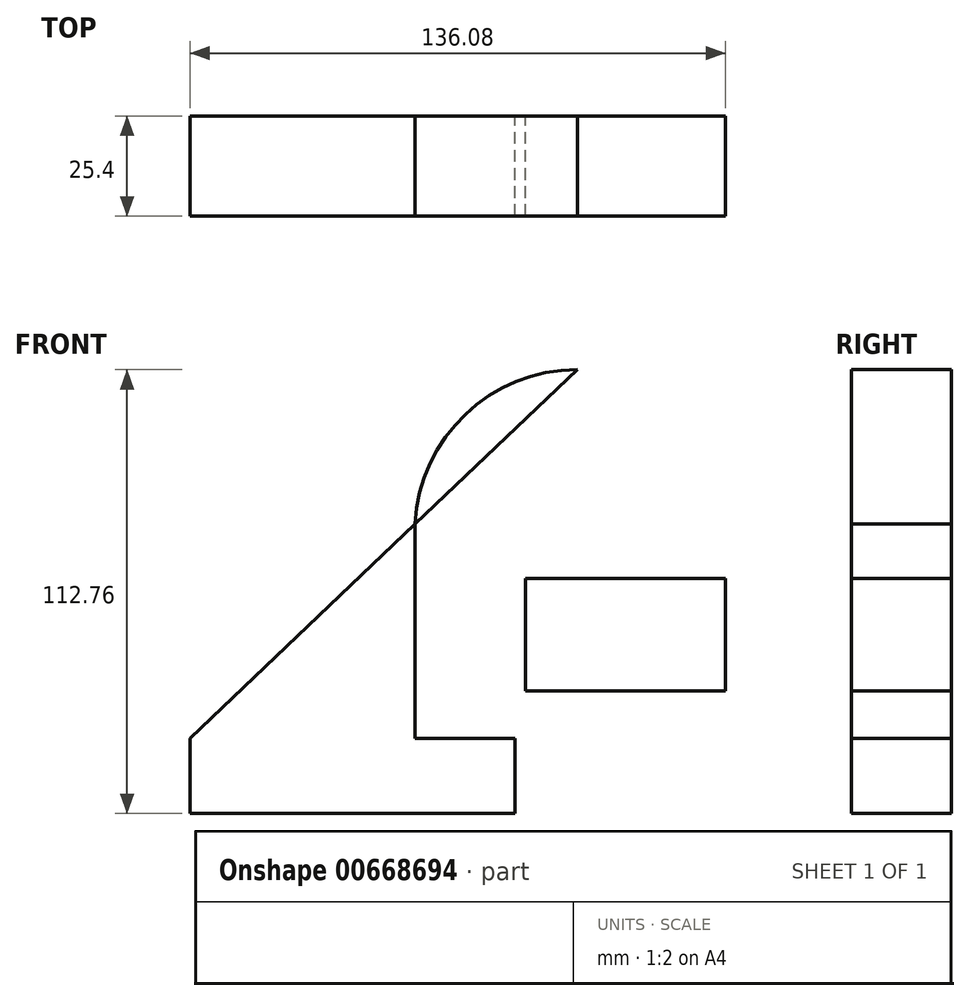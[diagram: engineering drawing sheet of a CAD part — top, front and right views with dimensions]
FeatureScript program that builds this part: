
annotation { "Feature Type Name" : "Feature", "Feature Type Description" : "" }
export const myFeature = defineFeature(function(context is Context, id is Id, definition is map)
    precondition{}
    {
        {
            var Q0;
            Q0=qCreatedBy(makeId("Front.planeOp"),FACE);
            var sketch = newSketch(context, id + "F0", { "sketchPlane" : qUnion([Q0])});
            skLineSegment(sketch, "E0.bottom", {"start": v(41.28, -9.52) * mm, "end": v(-41.28, -9.53) * mm});
            skLineSegment(sketch, "E0.top", {"start": v(41.27, 9.53) * mm, "end": v(-41.28, 9.53) * mm});
            skLineSegment(sketch, "E0.left", {"start": v(41.28, -9.53) * mm, "end": v(41.28, 9.53) * mm});
            skLineSegment(sketch, "E0.right", {"start": v(-41.28, -9.53) * mm, "end": v(-41.28, 9.53) * mm});
            skPoint(sketch, "E0.middle", {"position": v(0, 0) * mm});
            skLineSegment(sketch, "E1.bottom", {"start": v(94.8, 21.6) * mm, "end": v(44, 21.6) * mm});
            skLineSegment(sketch, "E1.top", {"start": v(94.8, 50.17) * mm, "end": v(44, 50.17) * mm});
            skLineSegment(sketch, "E1.left", {"start": v(94.8, 21.6) * mm, "end": v(94.8, 50.17) * mm});
            skLineSegment(sketch, "E1.right", {"start": v(44, 21.6) * mm, "end": v(44, 50.17) * mm});
            skPoint(sketch, "E1.middle", {"position": v(69.4, 35.89) * mm});
            skLineSegment(sketch, "E2", {"start": v(41.27, 9.53) * mm, "end": v(41.27, 61.93) * mm});
            skArc(sketch, "E3", {"start": v(41.27, 61.93) * mm, "mid": v(45.92, 73.15) * mm, "end": v(57.15, 77.8) * mm});
            skLineSegment(sketch, "E4", {"start": v(57.15, 77.8) * mm, "end": v(80.26, 77.8) * mm});
            skLineSegment(sketch, "E5.0", {"start": v(57.15, 103.23) * mm, "end": v(80.26, 103.23) * mm});
            skArc(sketch, "E5.1", {"start": v(15.85, 61.93) * mm, "mid": v(27.94, 91.13) * mm, "end": v(57.15, 103.23) * mm});
            skLineSegment(sketch, "E5.2", {"start": v(15.85, 9.53) * mm, "end": v(15.85, 61.93) * mm});
            skFitSpline(sketch, "E6", {"points": [v(-41.28, 9.53) * mm, v(57.15, 103.23) * mm], "startDerivative": vector(98.43, 93.7) * mm, "endDerivative": vector(98.43, 93.7) * mm});
            skSolve(sketch);
        }
        {
            var Q0;
            Q0 = qSketchRegion(id + "F0", true);
            extrude(context, id + "F1", {"entities" : qUnion([Q0]), "depth" : 25.4 * mm, "offsetDistance" : 25.4 * mm});
        }
    });
